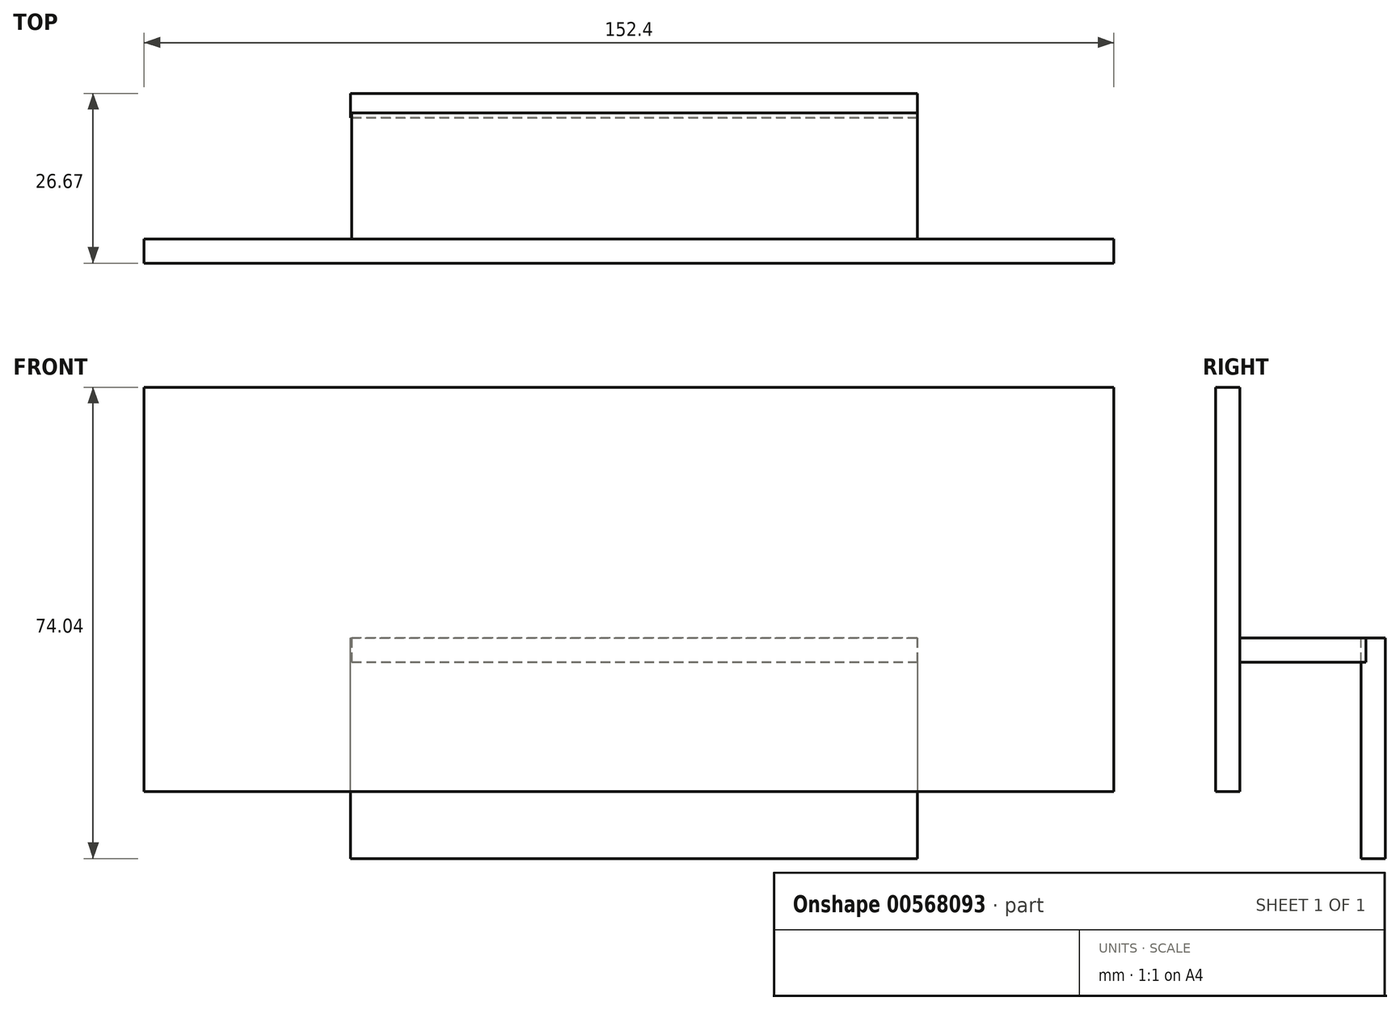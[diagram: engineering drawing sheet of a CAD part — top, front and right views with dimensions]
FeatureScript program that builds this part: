
annotation { "Feature Type Name" : "Feature", "Feature Type Description" : "" }
export const myFeature = defineFeature(function(context is Context, id is Id, definition is map)
    precondition{}
    {
        {
            var Q0;
            Q0=qCreatedBy(makeId("Front.planeOp"),FACE);
            var sketch = newSketch(context, id + "F0", { "sketchPlane" : qUnion([Q0])});
            skLineSegment(sketch, "E0", {"start": v(-73.01, 71.24) * mm, "end": v(-73.01, 7.74) * mm});
            skLineSegment(sketch, "E1", {"start": v(-73.01, 7.74) * mm, "end": v(79.39, 7.74) * mm});
            skLineSegment(sketch, "E2", {"start": v(79.39, 7.74) * mm, "end": v(79.39, 71.24) * mm});
            skLineSegment(sketch, "E3", {"start": v(79.39, 71.24) * mm, "end": v(-73.01, 71.24) * mm});
            skSolve(sketch);
        }
        {
            var Q0;
            Q0 = qSketchRegion(id + "F0", true);
            extrude(context, id + "F1", {"entities" : qUnion([Q0]), "depth" : 3.8 * mm, "offsetDistance" : 25.4 * mm});
        }
        {
            var Q0;
            Q0=qCreatedBy(makeId("Top.planeOp"),FACE);
            cPlane(context, id + "F2", {"entities" : qUnion([Q0]), "cplaneType" : CPlaneType.OFFSET, "offset" : 28.04 * mm, "width" : 152.4 * mm, "height" : 152.4 * mm});
        }
        {
            var Q0;
            Q0=qCreatedBy(id+"F2.planeOp",FACE);
            var sketch = newSketch(context, id + "F3", { "sketchPlane" : qUnion([Q0])});
            skLineSegment(sketch, "E4.bottom", {"start": v(48.54, 0) * mm, "end": v(-40.36, 0) * mm});
            skLineSegment(sketch, "E4.top", {"start": v(48.54, 19.81) * mm, "end": v(-40.36, 19.81) * mm});
            skLineSegment(sketch, "E4.left", {"start": v(48.54, 0) * mm, "end": v(48.54, 19.81) * mm});
            skLineSegment(sketch, "E4.right", {"start": v(-40.36, 0) * mm, "end": v(-40.36, 19.81) * mm});
            skSolve(sketch);
        }
        {
            var Q0;
            Q0=makeQuery(id+"F3.imprint","IMPRINT",FACE,{"disambiguationData":[TD([[makeQuery(id+"F3.imprint","IMPRINT",EDGE,{"derivedFrom":sQuery(id+"F3.wireOp",EDGE,"E4.bottom")}),-1.0]])]});
            extrude(context, id + "F4", {"entities" : qUnion([Q0]), "operationType" : NewBodyOperationType.ADD, "depth" : 3.8 * mm, "offsetDistance" : 25.4 * mm});
        }
        {
            var Q0;
            Q0=qCreatedBy(makeId("Front.planeOp"),FACE);
            cPlane(context, id + "F5", {"entities" : qUnion([Q0]), "cplaneType" : CPlaneType.OFFSET, "offset" : 22.86 * mm, "oppositeDirection" : true, "width" : 152.4 * mm, "height" : 152.4 * mm});
        }
        {
            var Q0;
            Q0=qCreatedBy(id+"F5.planeOp",FACE);
            var sketch = newSketch(context, id + "F6", { "sketchPlane" : qUnion([Q0])});
            skLineSegment(sketch, "E5", {"start": v(48.52, 31.83) * mm, "end": v(48.52, -2.8) * mm});
            skLineSegment(sketch, "E6", {"start": v(48.52, -2.8) * mm, "end": v(-40.58, -2.8) * mm});
            skLineSegment(sketch, "E7", {"start": v(-40.58, -2.8) * mm, "end": v(-40.58, 31.83) * mm});
            skLineSegment(sketch, "E8", {"start": v(-40.58, 31.83) * mm, "end": v(48.52, 31.83) * mm});
            skSolve(sketch);
        }
        {
            var Q0;
            Q0=makeQuery(id+"F6.imprint","IMPRINT",FACE,{"disambiguationData":[TD([[makeQuery(id+"F6.imprint","IMPRINT",EDGE,{"derivedFrom":sQuery(id+"F6.wireOp",EDGE,"E5")}),-1.0]])]});
            extrude(context, id + "F7", {"entities" : qUnion([Q0]), "operationType" : NewBodyOperationType.ADD, "depth" : 3.8 * mm, "offsetDistance" : 25.4 * mm});
        }
    });
